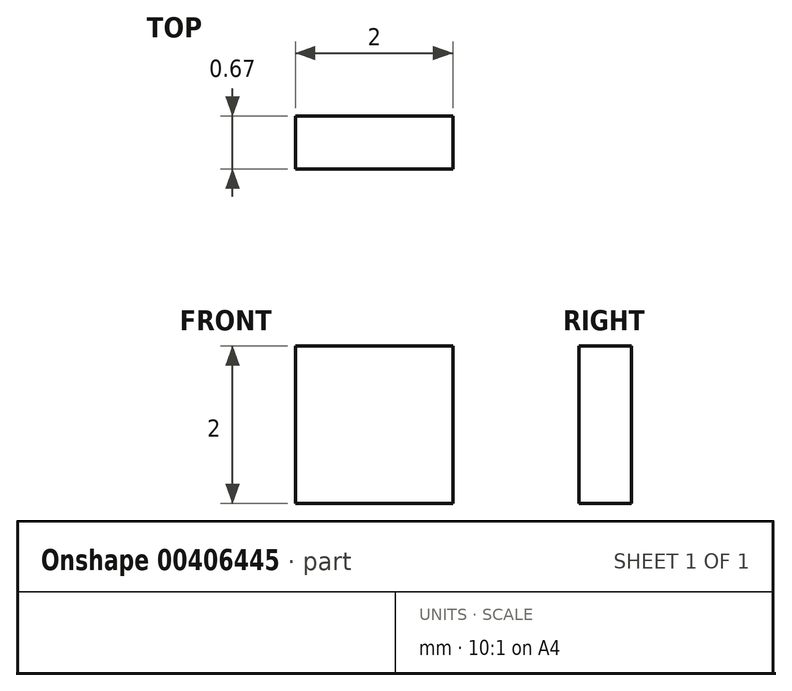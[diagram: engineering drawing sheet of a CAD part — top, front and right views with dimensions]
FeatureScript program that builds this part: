
annotation { "Feature Type Name" : "Feature", "Feature Type Description" : "" }
export const myFeature = defineFeature(function(context is Context, id is Id, definition is map)
    precondition{}
    {
        {
            var Q0;
            Q0=qCreatedBy(makeId("Top.planeOp"),FACE);
            var sketch = newSketch(context, id + "F0", { "sketchPlane" : qUnion([Q0])});
            skLineSegment(sketch, "E0.bottom", {"start": v(0, 0) * mm, "end": v(2, 0) * mm});
            skLineSegment(sketch, "E0.top", {"start": v(0, 0.67) * mm, "end": v(2, 0.67) * mm});
            skLineSegment(sketch, "E0.left", {"start": v(0, 0) * mm, "end": v(0, 0.67) * mm});
            skLineSegment(sketch, "E0.right", {"start": v(2, 0) * mm, "end": v(2, 0.67) * mm});
            skSolve(sketch);
        }
        {
            var Q0;
            Q0=makeQuery(id+"F0.imprint","IMPRINT",FACE,{"disambiguationData":[TD([[makeQuery(id+"F0.imprint","IMPRINT",EDGE,{"derivedFrom":sQuery(id+"F0.wireOp",EDGE,"E0.bottom")}),1.0]])]});
            extrude(context, id + "F1", {"entities" : qUnion([Q0]), "depth" : 2 * mm});
        }
    });
